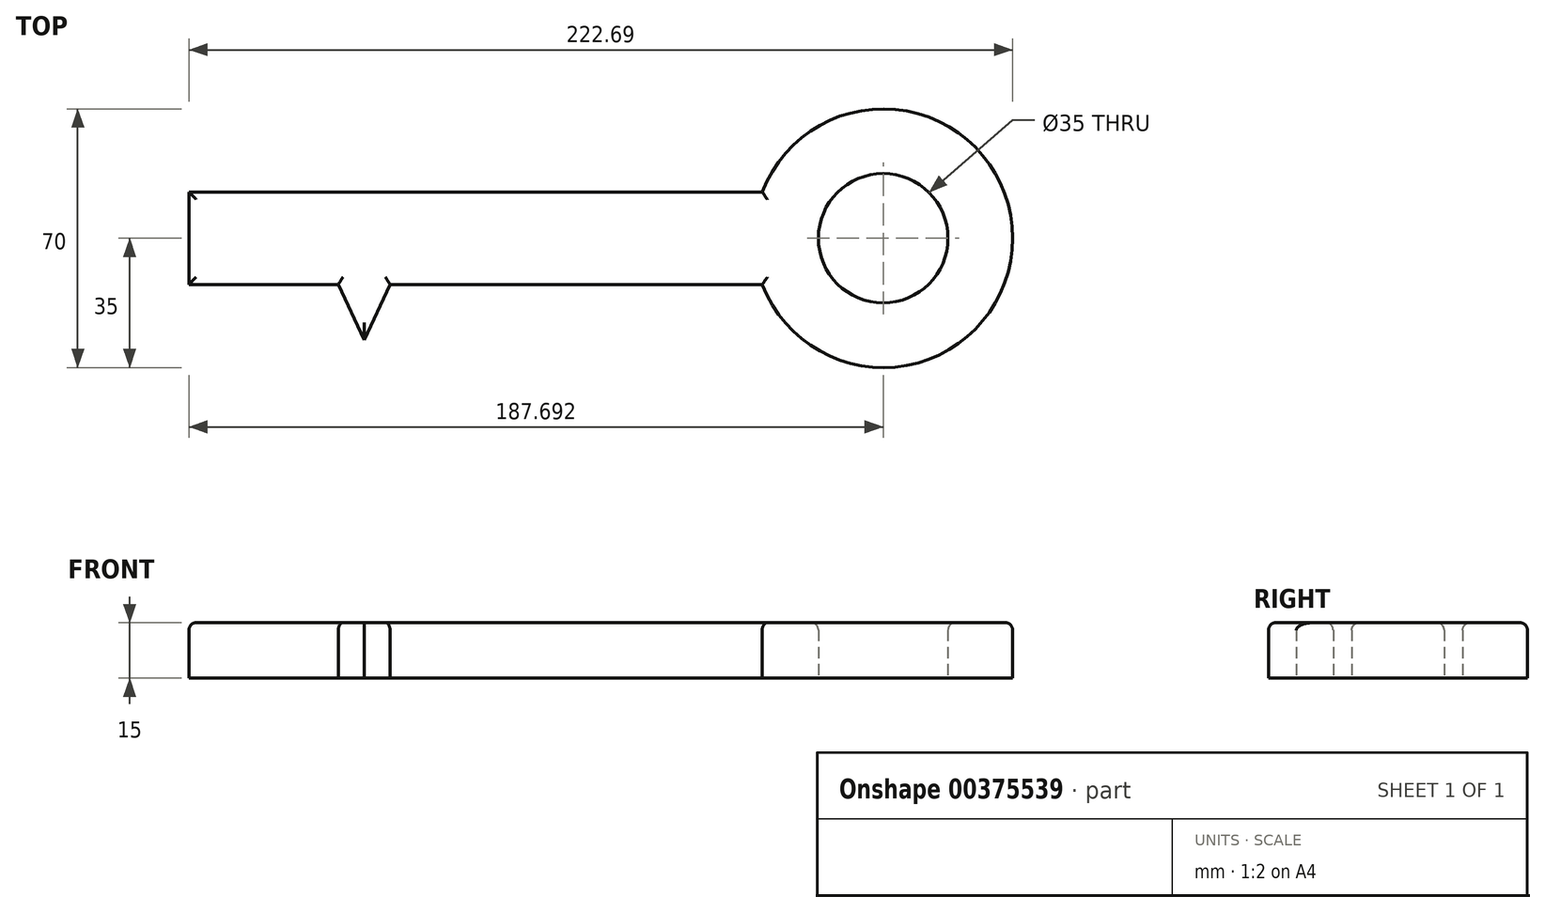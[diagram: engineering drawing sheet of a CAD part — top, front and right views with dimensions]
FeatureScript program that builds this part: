
annotation { "Feature Type Name" : "Feature", "Feature Type Description" : "" }
export const myFeature = defineFeature(function(context is Context, id is Id, definition is map)
    precondition{}
    {
        {
            var Q0;
            Q0=qCreatedBy(makeId("Top.planeOp"),FACE);
            var sketch = newSketch(context, id + "F0", { "sketchPlane" : qUnion([Q0])});
            skLineSegment(sketch, "E0.bottom", {"start": v(-70.59, 40) * mm, "end": v(84.41, 40) * mm});
            skLineSegment(sketch, "E0.top", {"start": v(-70.59, 15) * mm, "end": v(84.41, 15) * mm});
            skLineSegment(sketch, "E0.left", {"start": v(-70.59, 40) * mm, "end": v(-70.59, 15) * mm});
            skLineSegment(sketch, "E0.right", {"start": v(84.41, 40) * mm, "end": v(84.41, 15) * mm});
            skLineSegment(sketch, "E1.bottom", {"start": v(-70.59, 15) * mm, "end": v(-60.59, 15) * mm});
            skLineSegment(sketch, "E1.top", {"start": v(-70.59, -15) * mm, "end": v(-60.59, -15) * mm});
            skLineSegment(sketch, "E1.left", {"start": v(-70.59, 15) * mm, "end": v(-70.59, -15) * mm});
            skLineSegment(sketch, "E1.right", {"start": v(-60.59, 15) * mm, "end": v(-60.59, -15) * mm});
            skLineSegment(sketch, "E2.bottom", {"start": v(-50.59, 15) * mm, "end": v(-40.2, 15) * mm});
            skLineSegment(sketch, "E2.top", {"start": v(-50.59, 0) * mm, "end": v(-40.2, 0) * mm});
            skLineSegment(sketch, "E2.left", {"start": v(-50.59, 15) * mm, "end": v(-50.59, 0) * mm});
            skLineSegment(sketch, "E2.right", {"start": v(-40.2, 15) * mm, "end": v(-40.2, 0) * mm});
            skLineSegment(sketch, "E3", {"start": v(-30.2, 15) * mm, "end": v(-23.2, 0) * mm});
            skLineSegment(sketch, "E4", {"start": v(-23.2, 0) * mm, "end": v(-16.2, 15) * mm});
            skArc(sketch, "E5", {"start": v(84.41, 15) * mm, "mid": v(152.1, 27.5) * mm, "end": v(84.41, 40) * mm});
            skCircle(sketch, "E6", {"center": v(117.1, 27.5) * mm, "radius": 17.5 * mm});
            skLineSegment(sketch, "E7", {"start": v(117.1, 27.5) * mm, "end": v(-70.59, 27.5) * mm, "construction": true});
            skSolve(sketch);
        }
        {
            var Q0;
            Q0=makeQuery(id+"F0.imprint","IMPRINT",FACE,{"disambiguationData":[TD([[makeQuery(id+"F0.imprint","IMPRINT",EDGE,{"derivedFrom":sQuery(id+"F0.wireOp",EDGE,"E0.right")}),1.0]])]});
            var Q1;
            {var subQ0=sQuery(id+"F0.wireOp",EDGE,"E3");Q1=makeQuery(id+"F0.imprint","IMPRINT",FACE,{"disambiguationData":[TD([[makeQuery(id+"F0.imprint","IMPRINT",EDGE,{"derivedFrom":subQ0}),1.0]])]});}
            var Q2;
            Q2=makeQuery(id+"F0.imprint","IMPRINT",FACE,{"disambiguationData":[TD([[makeQuery(id+"F0.imprint","IMPRINT",EDGE,{"derivedFrom":sQuery(id+"F0.wireOp",EDGE,"E2.bottom")}),-1.0]])]});
            var Q3;
            Q3=makeQuery(id+"F0.imprint","IMPRINT",FACE,{"disambiguationData":[TD([[makeQuery(id+"F0.imprint","IMPRINT",EDGE,{"derivedFrom":sQuery(id+"F0.wireOp",EDGE,"E1.bottom")}),-1.0]])]});
            var Q4;
            Q4=makeQuery(id+"F0.imprint","IMPRINT",FACE,{"disambiguationData":[TD([[makeQuery(id+"F0.imprint","IMPRINT",EDGE,{"derivedFrom":sQuery(id+"F0.wireOp",EDGE,"E0.bottom")}),-1.0]])]});
            extrude(context, id + "F1", {"entities" : qUnion([Q0, Q1, Q2, Q3, Q4]), "depth" : 15 * mm});
        }
        {
            var Q0;
            Q0=makeQuery(id+"F1.opExtrude","CAP_EDGE",EDGE,{"disambiguationData":[OSD([sQuery(id+"F0.wireOp",EDGE,"E0.left"),sQuery(id+"F0.wireOp",EDGE,"E1.left")])],"isStart":false});
            var Q1;
            Q1=makeQuery(id+"F1.opExtrude","CAP_EDGE",EDGE,{"disambiguationData":[OSD([sQuery(id+"F0.wireOp",EDGE,"E0.bottom")])],"isStart":false});
            var Q2;
            Q2=makeQuery(id+"F1.opExtrude","CAP_EDGE",EDGE,{"disambiguationData":[OSD([sQuery(id+"F0.wireOp",EDGE,"E1.top")])],"isStart":false});
            var Q3;
            Q3=makeQuery(id+"F1.opExtrude","CAP_EDGE",EDGE,{"disambiguationData":[OSD([sQuery(id+"F0.wireOp",EDGE,"E1.right")])],"isStart":false});
            var Q4;
            {var subQ0=sQuery(id+"F0.wireOp",EDGE,"E0.top");Q4=makeQuery(id+"F1.opExtrude","CAP_EDGE",EDGE,{"disambiguationData":[OSD([subQ0]),TDD([makeQuery(id+"F0.imprint","IMPRINT",EDGE,{"disambiguationData":[TD([[makeQuery(id+"F0.imprint","INTERSECT",VERTEX,{"derivedFrom":[subQ0,sQuery(id+"F0.wireOp",EDGE,"E1.bottom"),sQuery(id+"F0.wireOp",EDGE,"E1.right")]}),-1.0]])],"derivedFrom":subQ0})])],"isStart":false});}
            var Q5;
            Q5=makeQuery(id+"F1.opExtrude","CAP_EDGE",EDGE,{"disambiguationData":[OSD([sQuery(id+"F0.wireOp",EDGE,"E2.left")])],"isStart":false});
            var Q6;
            Q6=makeQuery(id+"F1.opExtrude","CAP_EDGE",EDGE,{"disambiguationData":[OSD([sQuery(id+"F0.wireOp",EDGE,"E6")])],"isStart":false});
            var Q7;
            Q7=makeQuery(id+"F1.opExtrude","CAP_EDGE",EDGE,{"disambiguationData":[OSD([sQuery(id+"F0.wireOp",EDGE,"E5")])],"isStart":false});
            var Q8;
            {var subQ0=sQuery(id+"F0.wireOp",EDGE,"E0.top");Q8=makeQuery(id+"F1.opExtrude","CAP_EDGE",EDGE,{"disambiguationData":[OSD([subQ0]),TDD([makeQuery(id+"F0.imprint","IMPRINT",EDGE,{"disambiguationData":[TD([[makeQuery(id+"F0.imprint","INTERSECT",VERTEX,{"derivedFrom":[subQ0,sQuery(id+"F0.wireOp",EDGE,"E4")]}),-1.0]])],"derivedFrom":subQ0})])],"isStart":false});}
            var Q9;
            Q9=makeQuery(id+"F1.opExtrude","CAP_EDGE",EDGE,{"disambiguationData":[OSD([sQuery(id+"F0.wireOp",EDGE,"E4")])],"isStart":false});
            var Q10;
            Q10=makeQuery(id+"F1.opExtrude","CAP_EDGE",EDGE,{"disambiguationData":[OSD([sQuery(id+"F0.wireOp",EDGE,"E3")])],"isStart":false});
            var Q11;
            {var subQ0=sQuery(id+"F0.wireOp",EDGE,"E0.top");Q11=makeQuery(id+"F1.opExtrude","CAP_EDGE",EDGE,{"disambiguationData":[OSD([subQ0]),TDD([makeQuery(id+"F0.imprint","IMPRINT",EDGE,{"disambiguationData":[TD([[makeQuery(id+"F0.imprint","INTERSECT",VERTEX,{"derivedFrom":[subQ0,sQuery(id+"F0.wireOp",EDGE,"E3")]}),1.0]])],"derivedFrom":subQ0})])],"isStart":false});}
            var Q12;
            Q12=makeQuery(id+"F1.opExtrude","CAP_EDGE",EDGE,{"disambiguationData":[OSD([sQuery(id+"F0.wireOp",EDGE,"E2.right")])],"isStart":false});
            var Q13;
            Q13=makeQuery(id+"F1.opExtrude","CAP_FACE",FACE,{"disambiguationData":[OSD([sQuery(id+"F0.wireOp",EDGE,"E0.bottom"),sQuery(id+"F0.wireOp",EDGE,"E0.top"),sQuery(id+"F0.wireOp",EDGE,"E0.left"),sQuery(id+"F0.wireOp",EDGE,"E1.top"),sQuery(id+"F0.wireOp",EDGE,"E1.left"),sQuery(id+"F0.wireOp",EDGE,"E1.right"),sQuery(id+"F0.wireOp",EDGE,"E2.top"),sQuery(id+"F0.wireOp",EDGE,"E2.left"),sQuery(id+"F0.wireOp",EDGE,"E2.right"),sQuery(id+"F0.wireOp",EDGE,"E3"),sQuery(id+"F0.wireOp",EDGE,"E4"),sQuery(id+"F0.wireOp",EDGE,"E5"),sQuery(id+"F0.wireOp",EDGE,"E6")])],"isStart":false});
            fillet(context, id + "F2", {"entities" : qUnion([Q0, Q1, Q2, Q3, Q4, Q5, Q6, Q7, Q8, Q9, Q10, Q11, Q12, Q13]), "radius" : 2 * mm, "tangentPropagation" : true, "allowEdgeOverflow" : false});
        }
    });
